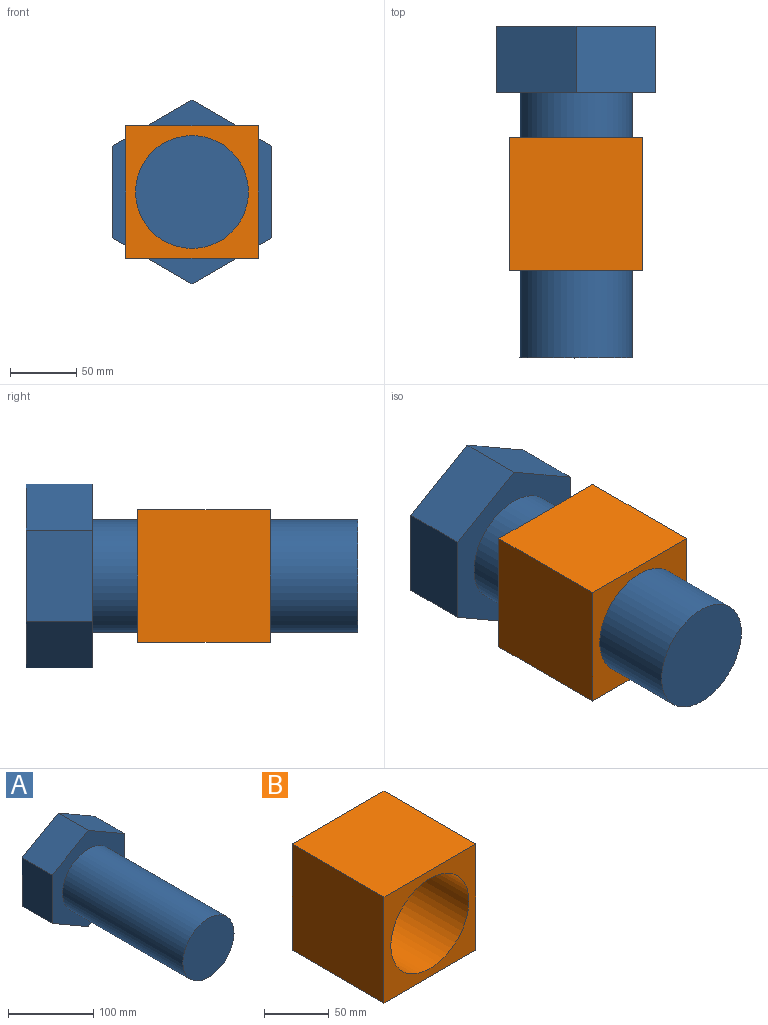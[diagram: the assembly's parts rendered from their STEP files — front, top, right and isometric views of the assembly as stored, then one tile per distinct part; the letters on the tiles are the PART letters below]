
ASSEMBLY  parts=2 mates=1
PART A: 10 faces, bbox 120x250x138.6 mm
  f0: plane 60x50mm, normal (-0.5,0,-0.87), area 3464.1mm2, adj f1,f5,f6,f7
  f1: plane 60x50mm, normal (0.5,0,-0.87), area 3464.1mm2, adj f0,f2,f6,f7
  f2: plane 69.28x50mm, normal (1,0,0), area 3464.1mm2, adj f1,f3,f6,f7
  f3: plane 60x50mm, normal (0.5,0,0.87), area 3464.1mm2, adj f2,f4,f6,f7
  f4: plane 60x50mm, normal (-0.5,0,0.87), area 3464.1mm2, adj f3,f5,f6,f7
  f5: plane 69.28x50mm, normal (-1,0,0), area 3464.1mm2, adj f0,f4,f6,f7
  f6: plane 138.56x120mm, normal (0,-1,0), area 6796.4mm2, adj f0,f1,f2,f3,f4,f5,f8
  f7: plane 138.56x120mm, normal (0,1,0), area 12470.8mm2, adj f0,f1,f2,f3,f4,f5
  f8: cylinder r=42.5mm len=200mm, axis (0,1,0), area 53406.4mm2, adj f6,f9
  f9: plane 85x85mm, normal (0,-1,0), area 5674.4mm2, adj f8
PART B: 7 faces, bbox 100x100x100 mm
  f0: plane 100x100mm, normal (0,0,1), area 10000mm2, adj f1,f4,f5,f6
  f1: plane 100x100mm, normal (-1,0,0), area 10000mm2, adj f0,f2,f5,f6
  f2: plane 100x100mm, normal (0,0,-1), area 10000mm2, adj f1,f4,f5,f6
  f3: cylinder r=42.5mm len=100mm, axis (0,1,0), area 26703.5mm2, adj f5,f6
  f4: plane 100x100mm, normal (1,0,0), area 10000mm2, adj f0,f2,f5,f6
  f5: plane 100x100mm, normal (0,-1,0), area 4325.5mm2, adj f0,f1,f2,f3,f4
  f6: plane 100x100mm, normal (0,1,0), area 4325.5mm2, adj f0,f1,f2,f3,f4
PLACE A t=(-34.1,100.99,17.46)mm
PLACE B t=(-34.1,-8.05,17.46)mm fixed
MATE slider A.f8 <-> B.f3  axis (0,1,0) through (-34.1,-24.01,17.46)mm
